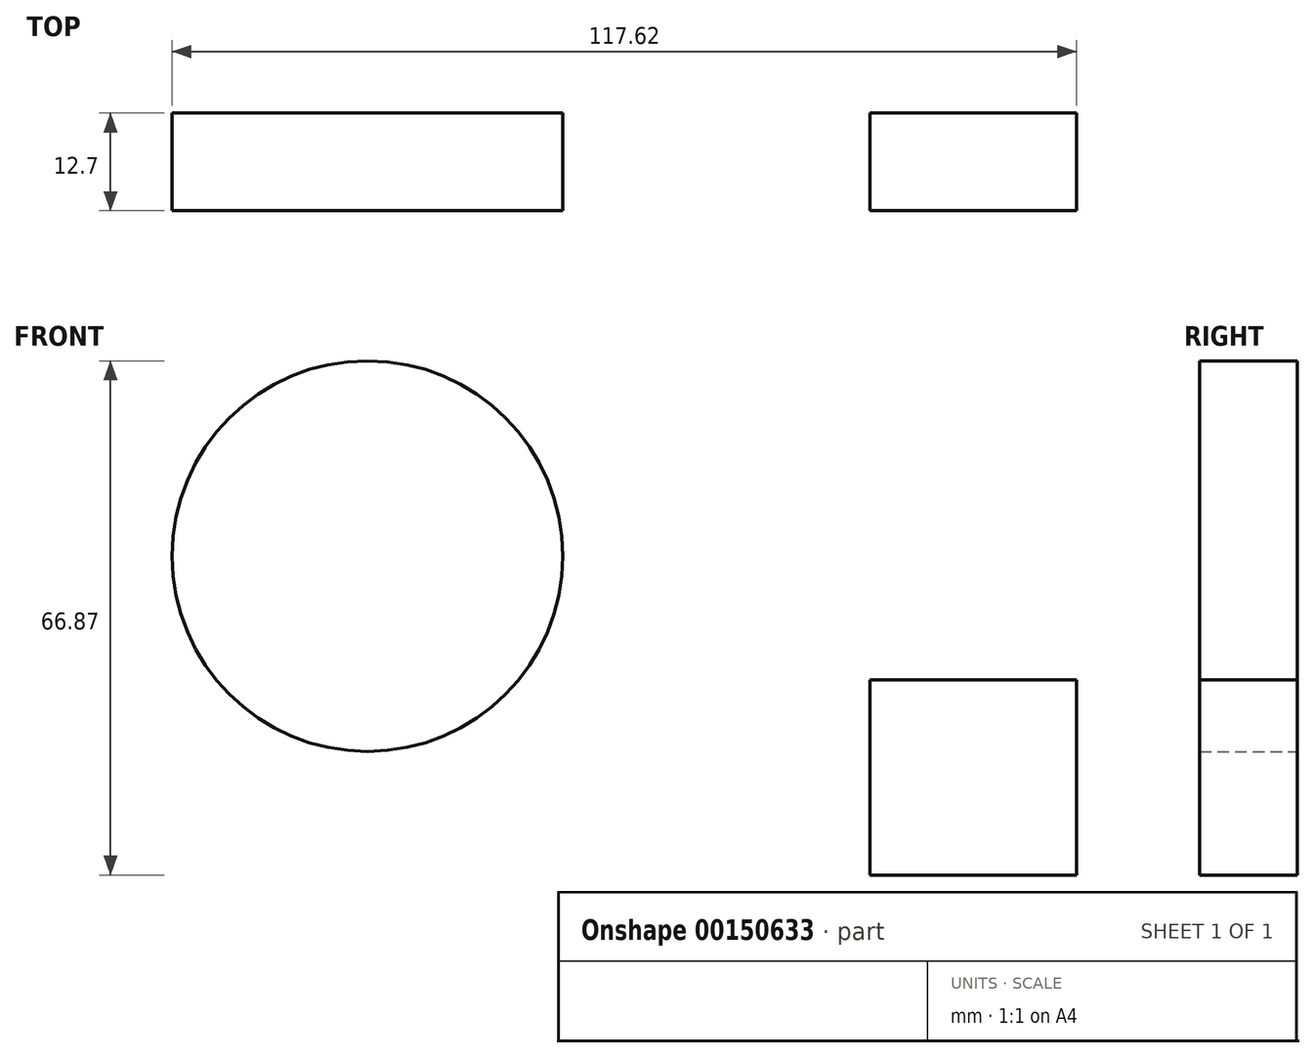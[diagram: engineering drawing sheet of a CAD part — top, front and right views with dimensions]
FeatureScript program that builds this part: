
annotation { "Feature Type Name" : "Feature", "Feature Type Description" : "" }
export const myFeature = defineFeature(function(context is Context, id is Id, definition is map)
    precondition{}
    {
        {
            var Q0;
            Q0=qCreatedBy(makeId("Front.planeOp"),FACE);
            var sketch = newSketch(context, id + "F0", { "sketchPlane" : qUnion([Q0])});
            skCircle(sketch, "E0", {"center": v(-39.2, 13.35) * mm, "radius": 25.4 * mm});
            skCircle(sketch, "E1", {"center": v(-39.2, 13.35) * mm, "radius": 22.23 * mm});
            skCircle(sketch, "E2", {"center": v(-39.2, 13.35) * mm, "radius": 6.35 * mm});
            skCircle(sketch, "E3", {"center": v(-39.58, 31.72) * mm, "radius": 1.59 * mm});
            skCircle(sketch, "E4", {"center": v(-38.06, -5.02) * mm, "radius": 1.59 * mm});
            skCircle(sketch, "E5", {"center": v(-58.7, 13.16) * mm, "radius": 1.59 * mm});
            skCircle(sketch, "E6", {"center": v(-21.2, 14.3) * mm, "radius": 1.59 * mm});
            skLineSegment(sketch, "E7.bottom", {"start": v(26.13, -2.72) * mm, "end": v(53.02, -2.72) * mm});
            skLineSegment(sketch, "E7.top", {"start": v(26.13, -28.12) * mm, "end": v(53.02, -28.12) * mm});
            skLineSegment(sketch, "E7.left", {"start": v(26.13, -2.72) * mm, "end": v(26.13, -28.12) * mm});
            skLineSegment(sketch, "E7.right", {"start": v(53.02, -2.72) * mm, "end": v(53.02, -28.12) * mm});
            skSolve(sketch);
        }
        {
            var Q0;
            Q0=makeQuery(id+"F0.imprint","IMPRINT",FACE,{"disambiguationData":[TD([[makeQuery(id+"F0.imprint","IMPRINT",EDGE,{"derivedFrom":sQuery(id+"F0.wireOp",EDGE,"E0")}),1.0]])]});
            var Q1;
            Q1=makeQuery(id+"F0.imprint","IMPRINT",FACE,{"disambiguationData":[TD([[makeQuery(id+"F0.imprint","IMPRINT",EDGE,{"derivedFrom":sQuery(id+"F0.wireOp",EDGE,"E1")}),1.0]])]});
            var Q2;
            Q2=makeQuery(id+"F0.imprint","IMPRINT",FACE,{"disambiguationData":[TD([[makeQuery(id+"F0.imprint","IMPRINT",EDGE,{"derivedFrom":sQuery(id+"F0.wireOp",EDGE,"E5")}),1.0]])]});
            var Q3;
            Q3=makeQuery(id+"F0.imprint","IMPRINT",FACE,{"disambiguationData":[TD([[makeQuery(id+"F0.imprint","IMPRINT",EDGE,{"derivedFrom":sQuery(id+"F0.wireOp",EDGE,"E4")}),1.0]])]});
            var Q4;
            Q4=makeQuery(id+"F0.imprint","IMPRINT",FACE,{"disambiguationData":[TD([[makeQuery(id+"F0.imprint","IMPRINT",EDGE,{"derivedFrom":sQuery(id+"F0.wireOp",EDGE,"E6")}),1.0]])]});
            var Q5;
            Q5=makeQuery(id+"F0.imprint","IMPRINT",FACE,{"disambiguationData":[TD([[makeQuery(id+"F0.imprint","IMPRINT",EDGE,{"derivedFrom":sQuery(id+"F0.wireOp",EDGE,"E3")}),1.0]])]});
            var Q6;
            Q6=makeQuery(id+"F0.imprint","IMPRINT",FACE,{"disambiguationData":[TD([[makeQuery(id+"F0.imprint","IMPRINT",EDGE,{"derivedFrom":sQuery(id+"F0.wireOp",EDGE,"E2")}),1.0]])]});
            var Q7;
            Q7=makeQuery(id+"F0.imprint","IMPRINT",FACE,{"disambiguationData":[TD([[makeQuery(id+"F0.imprint","IMPRINT",EDGE,{"derivedFrom":sQuery(id+"F0.wireOp",EDGE,"E7.bottom")}),-1.0]])]});
            extrude(context, id + "F1", {"entities" : qUnion([Q0, Q1, Q2, Q3, Q4, Q5, Q6, Q7]), "depth" : 12.7 * mm});
        }
    });
